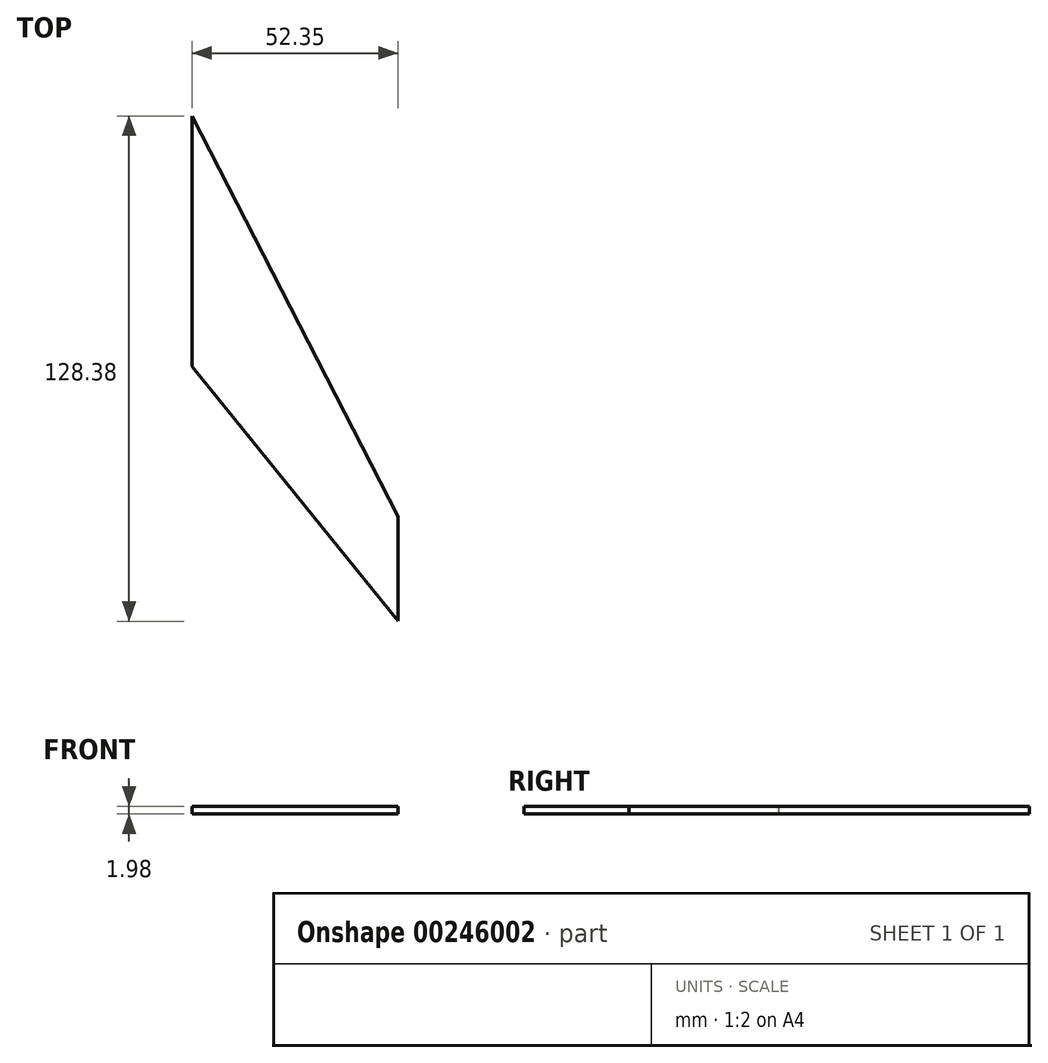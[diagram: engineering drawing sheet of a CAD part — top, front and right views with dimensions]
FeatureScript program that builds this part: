
annotation { "Feature Type Name" : "Feature", "Feature Type Description" : "" }
export const myFeature = defineFeature(function(context is Context, id is Id, definition is map)
    precondition{}
    {
        {
            var Q0;
            Q0=qCreatedBy(makeId("Top.planeOp"),FACE);
            var sketch = newSketch(context, id + "F0", { "sketchPlane" : qUnion([Q0])});
            skLineSegment(sketch, "E0", {"start": v(6.17, -51.39) * mm, "end": v(6.17, -24.75) * mm});
            skLineSegment(sketch, "E1", {"start": v(6.17, -24.75) * mm, "end": v(-46.18, 77) * mm});
            skLineSegment(sketch, "E2", {"start": v(-46.18, 77) * mm, "end": v(-46.18, 13.26) * mm});
            skLineSegment(sketch, "E3", {"start": v(-46.18, 13.26) * mm, "end": v(6.17, -51.39) * mm});
            skSolve(sketch);
        }
        {
            var Q0;
            Q0=makeQuery(id+"F0.imprint","IMPRINT",FACE,{"disambiguationData":[TD([[makeQuery(id+"F0.imprint","IMPRINT",EDGE,{"derivedFrom":sQuery(id+"F0.wireOp",EDGE,"E0")}),1.0]])]});
            extrude(context, id + "F1", {"entities" : qUnion([Q0]), "depth" : 1.98 * mm});
        }
    });
